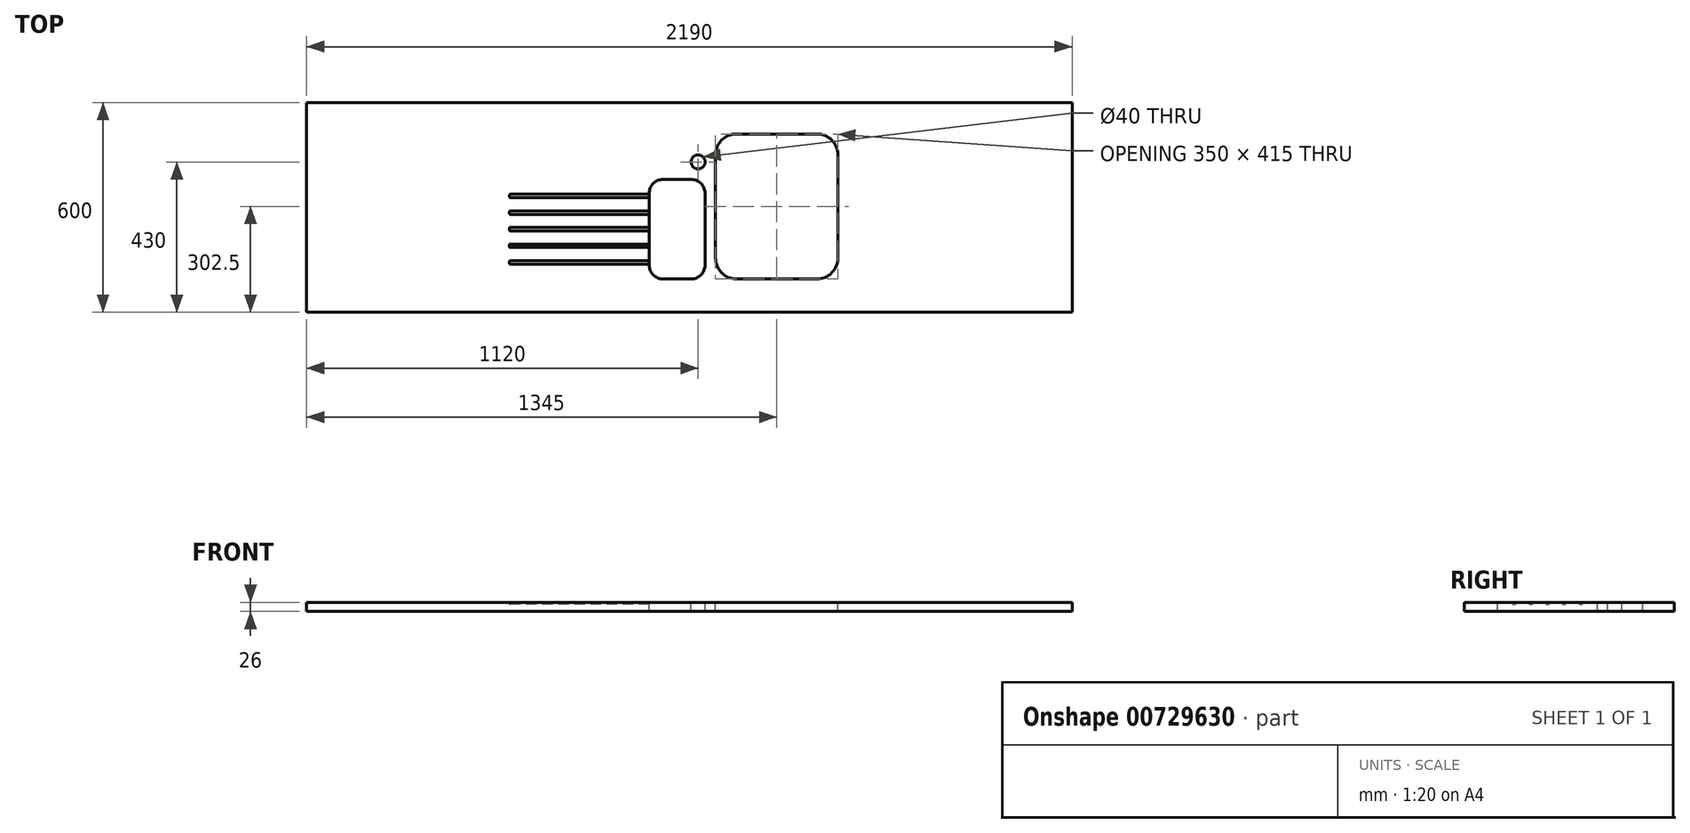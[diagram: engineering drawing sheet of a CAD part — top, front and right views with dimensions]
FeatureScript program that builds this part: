
annotation { "Feature Type Name" : "Feature", "Feature Type Description" : "" }
export const myFeature = defineFeature(function(context is Context, id is Id, definition is map)
    precondition{}
    {
        {
            var Q0;
            Q0=qCreatedBy(makeId("Top.planeOp"),FACE);
            var sketch = newSketch(context, id + "F0", { "sketchPlane" : qUnion([Q0])});
            skLineSegment(sketch, "E0.bottom", {"start": v(1095, -300) * mm, "end": v(-1095, -300) * mm});
            skLineSegment(sketch, "E0.top", {"start": v(1095, 300) * mm, "end": v(-1095, 300) * mm});
            skLineSegment(sketch, "E0.left", {"start": v(1095, -300) * mm, "end": v(1095, 300) * mm});
            skLineSegment(sketch, "E0.right", {"start": v(-1095, -300) * mm, "end": v(-1095, 300) * mm});
            skPoint(sketch, "E0.middle", {"position": v(0, 0) * mm});
            skSolve(sketch);
        }
        {
            var Q0;
            Q0 = qSketchRegion(id + "F0", true);
            extrude(context, id + "F1", {"entities" : qUnion([Q0]), "depth" : 26 * mm, "offsetDistance" : 25 * mm});
        }
        {
            var Q0;
            Q0=makeQuery(id+"F1.opExtrude","CAP_FACE",FACE,{"disambiguationData":[OSD([sQuery(id+"F0.wireOp",EDGE,"E0.bottom"),sQuery(id+"F0.wireOp",EDGE,"E0.top"),sQuery(id+"F0.wireOp",EDGE,"E0.left"),sQuery(id+"F0.wireOp",EDGE,"E0.right")])],"isStart":false});
            var sketch = newSketch(context, id + "F2", { "sketchPlane" : qUnion([Q0])});
            skLineSegment(sketch, "E1.bottom", {"start": v(365, -205) * mm, "end": v(135, -205) * mm});
            skLineSegment(sketch, "E1.top", {"start": v(365, 210) * mm, "end": v(135, 210) * mm});
            skLineSegment(sketch, "E1.left", {"start": v(425, -145) * mm, "end": v(425, 150) * mm});
            skLineSegment(sketch, "E1.right", {"start": v(75, -145) * mm, "end": v(75, 150) * mm});
            skLineSegment(sketch, "E2.bottom", {"start": v(5, -205) * mm, "end": v(-75, -205) * mm});
            skLineSegment(sketch, "E2.top", {"start": v(5, 80) * mm, "end": v(-75, 80) * mm});
            skLineSegment(sketch, "E2.left", {"start": v(45, -165) * mm, "end": v(45, 40) * mm});
            skLineSegment(sketch, "E2.right", {"start": v(-115, -165) * mm, "end": v(-115, 40) * mm});
            skPoint(sketch, "E2.middle", {"position": v(-35, -62.5) * mm});
            skPoint(sketch, "E3.visualSharp", {"position": v(425, 210) * mm});
            skArc(sketch, "E3.filletArc", {"start": v(425, 150) * mm, "mid": v(407.43, 192.43) * mm, "end": v(365, 210) * mm});
            skPoint(sketch, "E4.visualSharp", {"position": v(425, -205) * mm});
            skArc(sketch, "E4.filletArc", {"start": v(365, -205) * mm, "mid": v(407.43, -187.43) * mm, "end": v(425, -145) * mm});
            skPoint(sketch, "E5.visualSharp", {"position": v(75, 210) * mm});
            skArc(sketch, "E5.filletArc", {"start": v(135, 210) * mm, "mid": v(92.57, 192.43) * mm, "end": v(75, 150) * mm});
            skPoint(sketch, "E6.visualSharp", {"position": v(75, -205) * mm});
            skArc(sketch, "E6.filletArc", {"start": v(75, -145) * mm, "mid": v(92.57, -187.43) * mm, "end": v(135, -205) * mm});
            skPoint(sketch, "E7.visualSharp", {"position": v(45, 80) * mm});
            skArc(sketch, "E7.filletArc", {"start": v(45, 40) * mm, "mid": v(33.28, 68.28) * mm, "end": v(5, 80) * mm});
            skPoint(sketch, "E8.visualSharp", {"position": v(-115, 80) * mm});
            skArc(sketch, "E8.filletArc", {"start": v(-75, 80) * mm, "mid": v(-103.28, 68.28) * mm, "end": v(-115, 40) * mm});
            skPoint(sketch, "E9.visualSharp", {"position": v(45, -205) * mm});
            skArc(sketch, "E9.filletArc", {"start": v(5, -205) * mm, "mid": v(33.28, -193.28) * mm, "end": v(45, -165) * mm});
            skPoint(sketch, "E10.visualSharp", {"position": v(-115, -205) * mm});
            skArc(sketch, "E10.filletArc", {"start": v(-115, -165) * mm, "mid": v(-103.28, -193.28) * mm, "end": v(-75, -205) * mm});
            skSolve(sketch);
        }
        {
            var Q0;
            Q0 = qSketchRegion(id + "F2", true);
            extrude(context, id + "F3", {"entities" : qUnion([Q0]), "operationType" : NewBodyOperationType.REMOVE, "endBound" : BoundingType.THROUGH_ALL, "oppositeDirection" : true, "depth" : 25 * mm, "offsetDistance" : 25 * mm});
        }
        {
            var Q0;
            Q0=makeQuery(id+"F1.opExtrude","CAP_FACE",FACE,{"disambiguationData":[OSD([sQuery(id+"F0.wireOp",EDGE,"E0.bottom"),sQuery(id+"F0.wireOp",EDGE,"E0.top"),sQuery(id+"F0.wireOp",EDGE,"E0.left"),sQuery(id+"F0.wireOp",EDGE,"E0.right")])],"isStart":false});
            var sketch = newSketch(context, id + "F4", { "sketchPlane" : qUnion([Q0])});
            skLineSegment(sketch, "E11.bottom", {"start": v(-115, -152.5) * mm, "end": v(-512, -152.5) * mm});
            skLineSegment(sketch, "E11.top", {"start": v(-115, -162.5) * mm, "end": v(-512, -162.5) * mm});
            skLineSegment(sketch, "E11.left", {"start": v(-115, -152.5) * mm, "end": v(-115, -162.5) * mm});
            skLineSegment(sketch, "E11.right", {"start": v(-515, -152.5) * mm, "end": v(-515, -162.5) * mm});
            skLineSegment(sketch, "E12.0.1.0", {"start": v(-115, -105) * mm, "end": v(-512, -105) * mm});
            skLineSegment(sketch, "E12.0.1.1", {"start": v(-115, -115) * mm, "end": v(-512, -115) * mm});
            skLineSegment(sketch, "E12.0.1.2", {"start": v(-115, -105) * mm, "end": v(-115, -115) * mm});
            skLineSegment(sketch, "E12.0.1.3", {"start": v(-515, -108) * mm, "end": v(-515, -112) * mm});
            skLineSegment(sketch, "E12.0.2.0", {"start": v(-115, -57.5) * mm, "end": v(-512, -57.5) * mm});
            skLineSegment(sketch, "E12.0.2.1", {"start": v(-115, -67.5) * mm, "end": v(-512, -67.5) * mm});
            skLineSegment(sketch, "E12.0.2.2", {"start": v(-115, -57.5) * mm, "end": v(-115, -67.5) * mm});
            skLineSegment(sketch, "E12.0.2.3", {"start": v(-515, -60.5) * mm, "end": v(-515, -64.5) * mm});
            skLineSegment(sketch, "E12.0.3.0", {"start": v(-115, -10) * mm, "end": v(-512, -10) * mm});
            skLineSegment(sketch, "E12.0.3.1", {"start": v(-115, -20) * mm, "end": v(-512, -20) * mm});
            skLineSegment(sketch, "E12.0.3.2", {"start": v(-115, -10) * mm, "end": v(-115, -20) * mm});
            skLineSegment(sketch, "E12.0.3.3", {"start": v(-515, -13) * mm, "end": v(-515, -17) * mm});
            skLineSegment(sketch, "E12.0.4.0", {"start": v(-115, 37.5) * mm, "end": v(-512, 37.5) * mm});
            skLineSegment(sketch, "E12.0.4.1", {"start": v(-115, 27.5) * mm, "end": v(-512, 27.5) * mm});
            skLineSegment(sketch, "E12.0.4.2", {"start": v(-115, 37.5) * mm, "end": v(-115, 27.5) * mm});
            skLineSegment(sketch, "E12.0.4.3", {"start": v(-515, 34.5) * mm, "end": v(-515, 30.5) * mm});
            skLineSegment(sketch, "E12.direction1", {"start": v(-735, -162.5) * mm, "end": v(-515, -162.5) * mm, "construction": true});
            skLineSegment(sketch, "E12.direction2", {"start": v(-515, -159.5) * mm, "end": v(-515, -155.5) * mm, "construction": true});
            skPoint(sketch, "E13.newPointA", {"position": v(-515, -152.5) * mm});
            skPoint(sketch, "E13.newPointB", {"position": v(-515, -115) * mm});
            skArc(sketch, "E13.filletArc", {"start": v(-512, -152.5) * mm, "mid": v(-514.12, -153.38) * mm, "end": v(-515, -155.5) * mm});
            skPoint(sketch, "E14.visualSharp", {"position": v(-515, -162.5) * mm});
            skArc(sketch, "E14.filletArc", {"start": v(-515, -159.5) * mm, "mid": v(-514.12, -161.62) * mm, "end": v(-512, -162.5) * mm});
            skPoint(sketch, "E15.visualSharp", {"position": v(-515, -105) * mm});
            skArc(sketch, "E15.filletArc", {"start": v(-512, -105) * mm, "mid": v(-514.12, -105.88) * mm, "end": v(-515, -108) * mm});
            skArc(sketch, "E16.filletArc", {"start": v(-515, -112) * mm, "mid": v(-514.12, -114.12) * mm, "end": v(-512, -115) * mm});
            skPoint(sketch, "E17.visualSharp", {"position": v(-515, -57.5) * mm});
            skArc(sketch, "E17.filletArc", {"start": v(-512, -57.5) * mm, "mid": v(-514.12, -58.38) * mm, "end": v(-515, -60.5) * mm});
            skPoint(sketch, "E18.visualSharp", {"position": v(-515, -67.5) * mm});
            skArc(sketch, "E18.filletArc", {"start": v(-515, -64.5) * mm, "mid": v(-514.12, -66.62) * mm, "end": v(-512, -67.5) * mm});
            skPoint(sketch, "E19.visualSharp", {"position": v(-515, 37.5) * mm});
            skArc(sketch, "E19.filletArc", {"start": v(-512, 37.5) * mm, "mid": v(-514.12, 36.62) * mm, "end": v(-515, 34.5) * mm});
            skPoint(sketch, "E20.visualSharp", {"position": v(-515, 27.5) * mm});
            skArc(sketch, "E20.filletArc", {"start": v(-515, 30.5) * mm, "mid": v(-514.12, 28.38) * mm, "end": v(-512, 27.5) * mm});
            skPoint(sketch, "E21.visualSharp", {"position": v(-515, -10) * mm});
            skArc(sketch, "E21.filletArc", {"start": v(-512, -10) * mm, "mid": v(-514.12, -10.88) * mm, "end": v(-515, -13) * mm});
            skPoint(sketch, "E22.visualSharp", {"position": v(-515, -20) * mm});
            skArc(sketch, "E22.filletArc", {"start": v(-515, -17) * mm, "mid": v(-514.12, -19.12) * mm, "end": v(-512, -20) * mm});
            skSolve(sketch);
        }
        {
            var Q0;
            Q0 = qSketchRegion(id + "F4", true);
            extrude(context, id + "F5", {"entities" : qUnion([Q0]), "operationType" : NewBodyOperationType.REMOVE, "oppositeDirection" : true, "depth" : 6 * mm, "offsetDistance" : 25 * mm});
        }
        {
            var Q0;
            Q0=makeQuery(id+"F5.boolean.opBoolean","COPY",EDGE,{"derivedFrom":makeQuery(id+"F5.opExtrude","CAP_EDGE",EDGE,{"disambiguationData":[OSD([sQuery(id+"F4.wireOp",EDGE,"E12.0.4.0")])],"isStart":false})});
            var Q1;
            Q1=makeQuery(id+"F5.boolean.opBoolean","COPY",EDGE,{"derivedFrom":makeQuery(id+"F5.opExtrude","CAP_EDGE",EDGE,{"disambiguationData":[OSD([sQuery(id+"F4.wireOp",EDGE,"E12.0.3.0")])],"isStart":false})});
            var Q2;
            Q2=makeQuery(id+"F5.boolean.opBoolean","COPY",EDGE,{"derivedFrom":makeQuery(id+"F5.opExtrude","CAP_EDGE",EDGE,{"disambiguationData":[OSD([sQuery(id+"F4.wireOp",EDGE,"E12.0.2.0")])],"isStart":false})});
            var Q3;
            Q3=makeQuery(id+"F5.boolean.opBoolean","COPY",EDGE,{"derivedFrom":makeQuery(id+"F5.opExtrude","CAP_EDGE",EDGE,{"disambiguationData":[OSD([sQuery(id+"F4.wireOp",EDGE,"E12.0.1.0")])],"isStart":false})});
            var Q4;
            Q4=makeQuery(id+"F5.boolean.opBoolean","COPY",EDGE,{"derivedFrom":makeQuery(id+"F5.opExtrude","CAP_EDGE",EDGE,{"disambiguationData":[OSD([sQuery(id+"F4.wireOp",EDGE,"E11.bottom")])],"isStart":false})});
            var Q5;
            Q5=makeQuery(id+"F5.boolean.opBoolean","COPY",EDGE,{"derivedFrom":makeQuery(id+"F5.opExtrude","CAP_EDGE",EDGE,{"disambiguationData":[OSD([sQuery(id+"F4.wireOp",EDGE,"E11.top")])],"isStart":false})});
            var Q6;
            Q6=makeQuery(id+"F5.boolean.opBoolean","COPY",EDGE,{"derivedFrom":makeQuery(id+"F5.opExtrude","CAP_EDGE",EDGE,{"disambiguationData":[OSD([sQuery(id+"F4.wireOp",EDGE,"E12.0.1.1")])],"isStart":false})});
            var Q7;
            Q7=makeQuery(id+"F5.boolean.opBoolean","COPY",EDGE,{"derivedFrom":makeQuery(id+"F5.opExtrude","CAP_EDGE",EDGE,{"disambiguationData":[OSD([sQuery(id+"F4.wireOp",EDGE,"E12.0.3.1")])],"isStart":false})});
            var Q8;
            Q8=makeQuery(id+"F5.boolean.opBoolean","COPY",EDGE,{"derivedFrom":makeQuery(id+"F5.opExtrude","CAP_EDGE",EDGE,{"disambiguationData":[OSD([sQuery(id+"F4.wireOp",EDGE,"E12.0.2.1")])],"isStart":false})});
            var Q9;
            Q9=makeQuery(id+"F5.boolean.opBoolean","COPY",EDGE,{"derivedFrom":makeQuery(id+"F5.opExtrude","CAP_EDGE",EDGE,{"disambiguationData":[OSD([sQuery(id+"F4.wireOp",EDGE,"E12.0.4.1")])],"isStart":false})});
            fillet(context, id + "F6", {"entities" : qUnion([Q0, Q1, Q2, Q3, Q4, Q5, Q6, Q7, Q8, Q9]), "radius" : 3 * mm, "tangentPropagation" : true, "allowEdgeOverflow" : false});
        }
        {
            var Q0;
            Q0=makeQuery(id+"F1.opExtrude","CAP_FACE",FACE,{"disambiguationData":[OSD([sQuery(id+"F0.wireOp",EDGE,"E0.bottom"),sQuery(id+"F0.wireOp",EDGE,"E0.top"),sQuery(id+"F0.wireOp",EDGE,"E0.left"),sQuery(id+"F0.wireOp",EDGE,"E0.right")])],"isStart":false});
            var sketch = newSketch(context, id + "F7", { "sketchPlane" : qUnion([Q0])});
            skCircle(sketch, "E23", {"center": v(25, 130) * mm, "radius": 20 * mm});
            skSolve(sketch);
        }
        {
            var Q0;
            Q0 = qSketchRegion(id + "F7", true);
            extrude(context, id + "F8", {"entities" : qUnion([Q0]), "operationType" : NewBodyOperationType.REMOVE, "endBound" : BoundingType.THROUGH_ALL, "oppositeDirection" : true, "depth" : 25 * mm, "offsetDistance" : 25 * mm});
        }
    });
